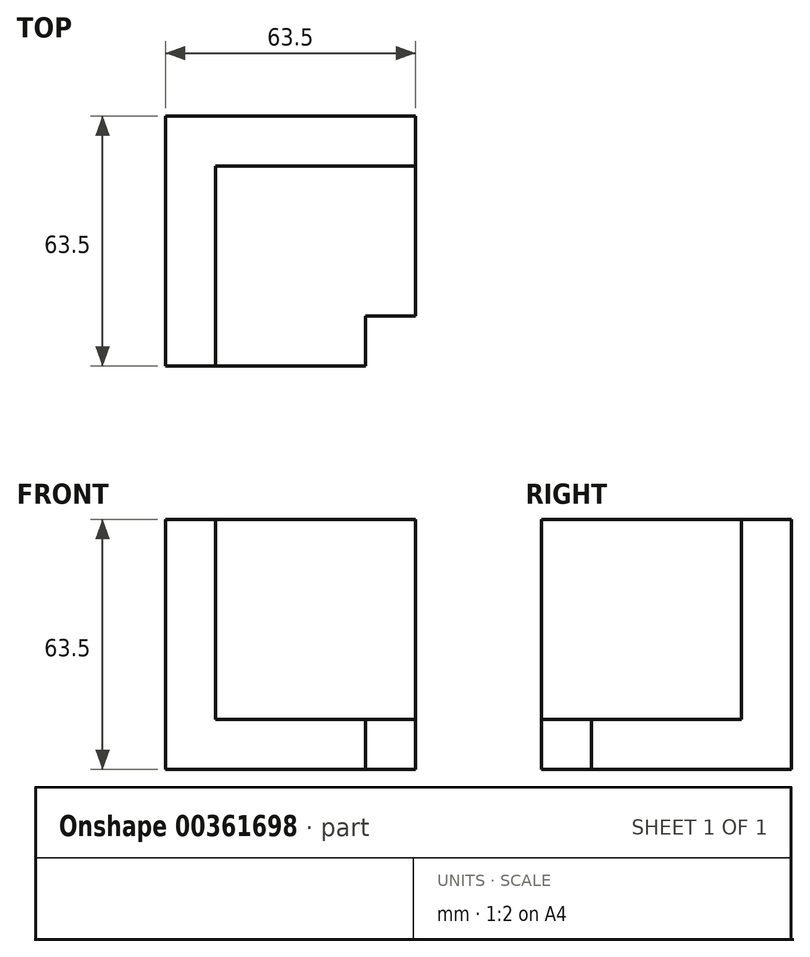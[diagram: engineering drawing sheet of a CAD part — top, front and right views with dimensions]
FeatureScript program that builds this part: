
annotation { "Feature Type Name" : "Feature", "Feature Type Description" : "" }
export const myFeature = defineFeature(function(context is Context, id is Id, definition is map)
    precondition{}
    {
        {
            var Q0;
            Q0=qCreatedBy(makeId("Front.planeOp"),FACE);
            var sketch = newSketch(context, id + "F0", { "sketchPlane" : qUnion([Q0])});
            skLineSegment(sketch, "E0.bottom", {"start": v(0, 0) * mm, "end": v(63.5, 0) * mm});
            skLineSegment(sketch, "E0.top", {"start": v(0, -63.5) * mm, "end": v(63.5, -63.5) * mm});
            skLineSegment(sketch, "E0.left", {"start": v(0, 0) * mm, "end": v(0, -63.5) * mm});
            skLineSegment(sketch, "E0.right", {"start": v(63.5, 0) * mm, "end": v(63.5, -63.5) * mm});
            skSolve(sketch);
        }
        {
            var Q0;
            Q0=makeQuery(id+"F0.imprint","IMPRINT",FACE,{"disambiguationData":[TD([[makeQuery(id+"F0.imprint","IMPRINT",EDGE,{"derivedFrom":sQuery(id+"F0.wireOp",EDGE,"E0.bottom")}),-1.0]])]});
            extrude(context, id + "F1", {"entities" : qUnion([Q0]), "depth" : 63.5 * mm});
        }
        {
            var Q0;
            Q0=makeQuery(id+"F1.opExtrude","CAP_FACE",FACE,{"disambiguationData":[OSD([sQuery(id+"F0.wireOp",EDGE,"E0.bottom"),sQuery(id+"F0.wireOp",EDGE,"E0.top"),sQuery(id+"F0.wireOp",EDGE,"E0.left"),sQuery(id+"F0.wireOp",EDGE,"E0.right")])],"isStart":false});
            var sketch = newSketch(context, id + "F2", { "sketchPlane" : qUnion([Q0])});
            skLineSegment(sketch, "E1.bottom", {"start": v(63.5, -50.8) * mm, "end": v(12.7, -50.8) * mm});
            skLineSegment(sketch, "E1.top", {"start": v(63.5, 0) * mm, "end": v(12.7, 0) * mm});
            skLineSegment(sketch, "E1.left", {"start": v(63.5, -50.8) * mm, "end": v(63.5, 0) * mm});
            skLineSegment(sketch, "E1.right", {"start": v(12.7, -50.8) * mm, "end": v(12.7, 0) * mm});
            skSolve(sketch);
        }
        {
            var Q0;
            Q0 = qSketchRegion(id + "F2", true);
            extrude(context, id + "F3", {"entities" : qUnion([Q0]), "operationType" : NewBodyOperationType.REMOVE, "oppositeDirection" : true, "depth" : 50.8 * mm});
        }
        {
            var Q0;
            Q0=makeQuery(id+"F1.opExtrude","CAP_FACE",FACE,{"disambiguationData":[OSD([sQuery(id+"F0.wireOp",EDGE,"E0.bottom"),sQuery(id+"F0.wireOp",EDGE,"E0.top"),sQuery(id+"F0.wireOp",EDGE,"E0.left"),sQuery(id+"F0.wireOp",EDGE,"E0.right")])],"isStart":false});
            var sketch = newSketch(context, id + "F4", { "sketchPlane" : qUnion([Q0])});
            skLineSegment(sketch, "E2.bottom", {"start": v(63.5, -63.5) * mm, "end": v(50.8, -63.5) * mm});
            skLineSegment(sketch, "E2.top", {"start": v(63.5, -50.8) * mm, "end": v(50.8, -50.8) * mm});
            skLineSegment(sketch, "E2.left", {"start": v(63.5, -63.5) * mm, "end": v(63.5, -50.8) * mm});
            skLineSegment(sketch, "E2.right", {"start": v(50.8, -63.5) * mm, "end": v(50.8, -50.8) * mm});
            skSolve(sketch);
        }
        {
            var Q0;
            Q0 = qSketchRegion(id + "F4", true);
            extrude(context, id + "F5", {"entities" : qUnion([Q0]), "operationType" : NewBodyOperationType.REMOVE, "oppositeDirection" : true, "depth" : 12.7 * mm});
        }
    });
